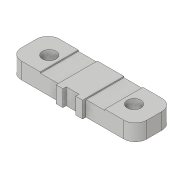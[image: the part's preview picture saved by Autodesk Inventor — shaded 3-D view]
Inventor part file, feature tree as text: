
AUTODESK INVENTOR PART (.ipt)
format: ipt  version: 2020 (Build 240168000, 168)  size: 152,576 bytes
history: native  units: in
note: dims shown in document units (in); Inventor stores cm internally (conversion verified against a paired STEP export)
features: extrude x6, sketch x6, mirror x2, plane x1, fillet x1
ambient origin geometry x8: Origin, YZ Plane, XZ Plane, XY Plane, X Axis, Y Axis, Z Axis, Center Point
bodies: Solid1 (feature_tree)
feature tree (16):
  extrude  "Extrusion1"  Depth=0.3937in
  extrude  "Extrusion2"  Depth=0.1575in TaperAngle=0.0deg
  plane  "Work Plane1"
  mirror  "Mirror1"
  fillet  "Fillet1"  [1 undecoded]
  extrude  "Extrusion3"  Depth=0.1181in
  extrude  "Extrusion4"  Depth=0.3937in
  mirror  "Mirror2"
  extrude  "Extrusion6"  Depth=0.315in
  extrude  "Extrusion7"  Depth=0.1181in
  sketch  "Sketch1"  dims[d0=1.2992in d1=0.3937in]
  sketch  "Sketch2"  dims[d2=0.1575in d3=0.0in d5=0.1575in d6=0.0in d7=-0.6496in]
  sketch  "Sketch3"  dims[d8=0.1181in d9=0.1417in]
  sketch  "Sketch4"  dims[d10=0.2756in d11=0.3937in]
  sketch  "Sketch6"  dims[d12=0.0118in d13=0.0in d14=0.315in]
  sketch  "Sketch7"  dims[d15=0.3937in d16=0.1181in d17=0.0118in d18=0.0in d21=0.3937in d22=0.0in d23=0.3937in d24=0.0in d19=0.0197in d20=0.0344in]
note: 1 required parameter value undecoded (feature->parameter linkage not recoverable at this tier; creation-order binding heuristic only, values carry confidence <= 0.55)
